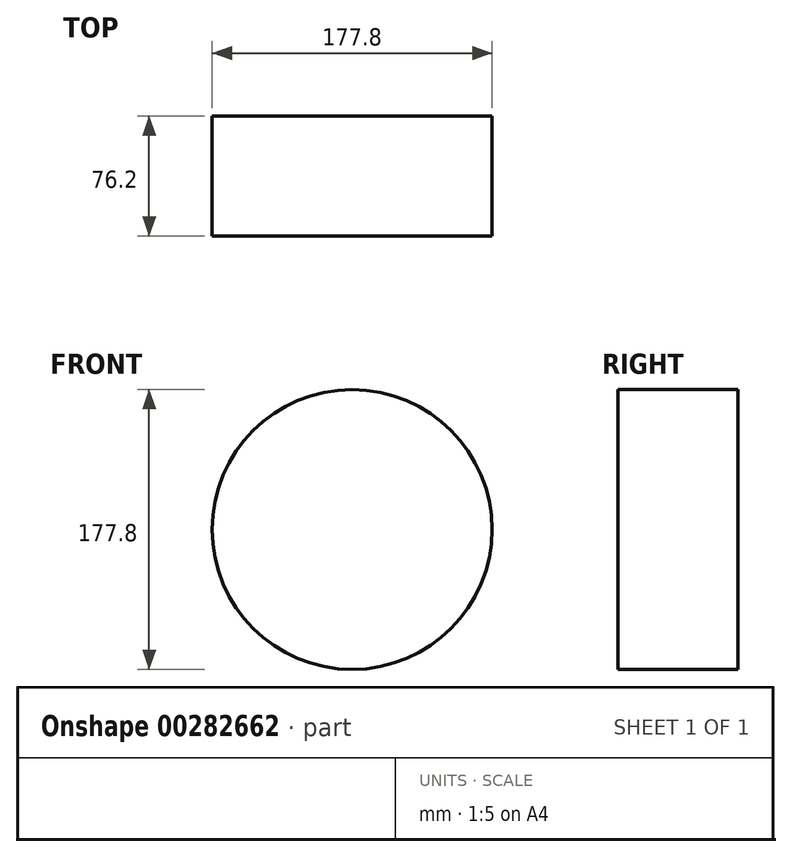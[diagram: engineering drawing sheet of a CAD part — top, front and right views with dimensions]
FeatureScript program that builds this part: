
annotation { "Feature Type Name" : "Feature", "Feature Type Description" : "" }
export const myFeature = defineFeature(function(context is Context, id is Id, definition is map)
    precondition{}
    {
        {
            var Q0;
            Q0=qCreatedBy(makeId("Front.planeOp"),FACE);
            var sketch = newSketch(context, id + "F0", { "sketchPlane" : qUnion([Q0])});
            skCircle(sketch, "E0", {"center": v(0, 0) * mm, "radius": 88.9 * mm});
            skSolve(sketch);
        }
        {
            var Q0;
            Q0=makeQuery(id+"F0.imprint","IMPRINT",FACE,{"disambiguationData":[TD([[makeQuery(id+"F0.imprint","IMPRINT",EDGE,{"derivedFrom":sQuery(id+"F0.wireOp",EDGE,"E0")}),1.0]])]});
            extrude(context, id + "F1", {"entities" : qUnion([Q0]), "depth" : 76.2 * mm});
        }
    });
